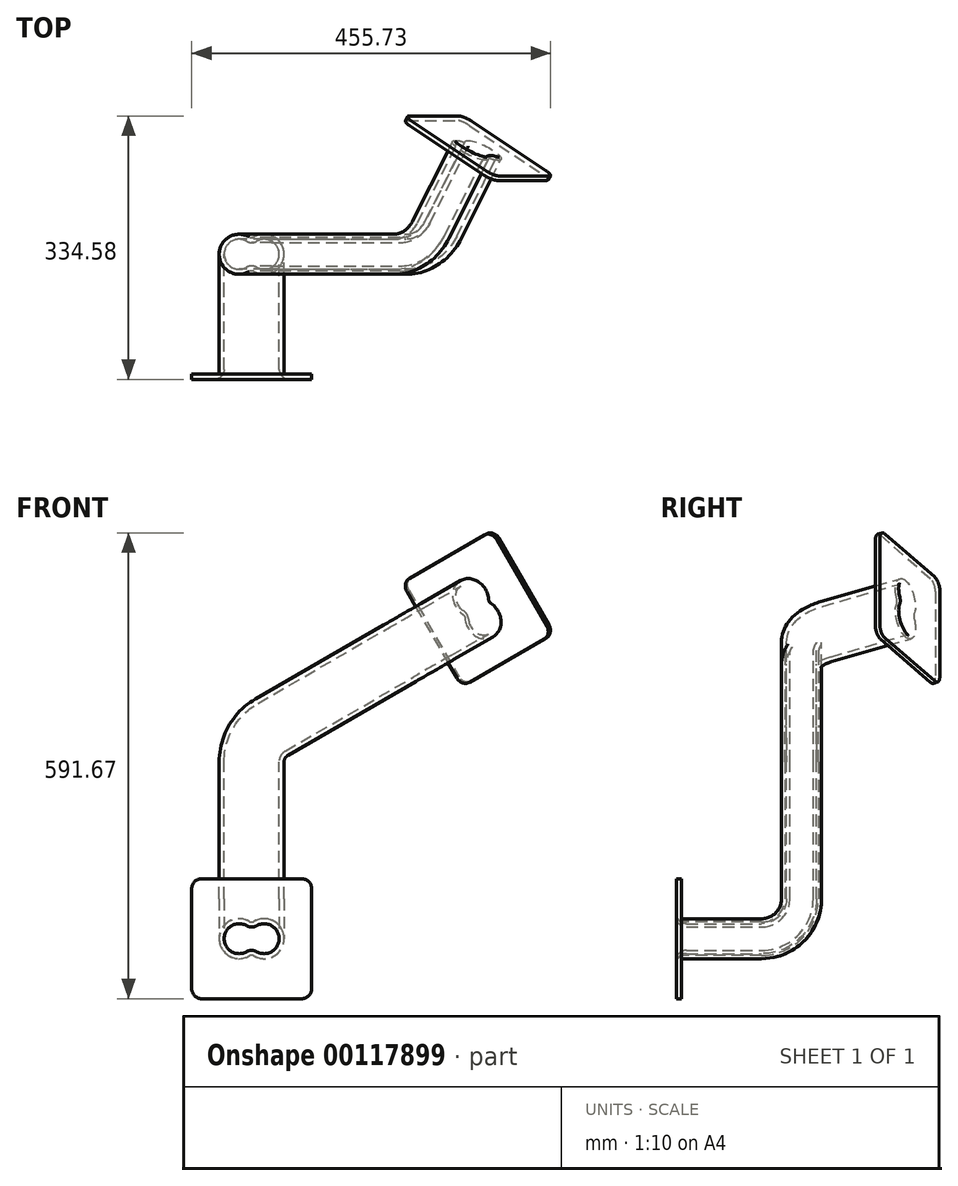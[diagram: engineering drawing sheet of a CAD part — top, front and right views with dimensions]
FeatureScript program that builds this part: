
annotation { "Feature Type Name" : "Feature", "Feature Type Description" : "" }
export const myFeature = defineFeature(function(context is Context, id is Id, definition is map)
    precondition{}
    {
        {
            var Q0;
            Q0=qCreatedBy(makeId("Right.planeOp"),FACE);
            var sketch = newSketch(context, id + "F0", { "sketchPlane" : qUnion([Q0])});
            skLineSegment(sketch, "E0", {"start": v(0, 0) * mm, "end": v(101.6, 0) * mm});
            skLineSegment(sketch, "E1", {"start": v(152.4, 50.8) * mm, "end": v(152.4, 177.8) * mm});
            skPoint(sketch, "E2.visualSharp", {"position": v(152.4, 0) * mm});
            skArc(sketch, "E2.filletArc", {"start": v(101.6, 0) * mm, "mid": v(137.52, 14.88) * mm, "end": v(152.4, 50.8) * mm});
            skSolve(sketch);
        }
        {
            var Q0;
            Q0=qCreatedBy(makeId("Front.planeOp"),FACE);
            var Q1;
            Q1=sQuery(id+"F0.wireOp",VERTEX,"E1.end");
            cPlane(context, id + "F1", {"entities" : qUnion([Q0, Q1]), "cplaneType" : CPlaneType.PLANE_POINT, "offset" : 25.4 * mm, "width" : 152.4 * mm, "height" : 152.4 * mm});
        }
        {
            var Q0;
            Q0=qCreatedBy(id+"F1.planeOp",FACE);
            var sketch = newSketch(context, id + "F2", { "sketchPlane" : qUnion([Q0])});
            skLineSegment(sketch, "E3", {"start": v(0, 177.8) * mm, "end": v(0, 224.67) * mm});
            skLineSegment(sketch, "E4", {"start": v(25.4, 268.66) * mm, "end": v(153.98, 342.9) * mm});
            skPoint(sketch, "E5.visualSharp", {"position": v(0, 254) * mm});
            skArc(sketch, "E5.filletArc", {"start": v(25.4, 268.66) * mm, "mid": v(6.8, 250.07) * mm, "end": v(0, 224.67) * mm});
            skSolve(sketch);
        }
        {
            var Q0;
            Q0=sQuery(id+"F2.wireOp",EDGE,"E4");
            cPlane(context, id + "F3", {"entities" : qUnion([Q0]), "cplaneType" : CPlaneType.LINE_ANGLE, "offset" : 25.4 * mm, "angle" : 90 * degree, "width" : 152.4 * mm, "height" : 152.4 * mm});
        }
        {
            var Q0;
            Q0=qCreatedBy(id+"F3.planeOp",FACE);
            var sketch = newSketch(context, id + "F4", { "sketchPlane" : qUnion([Q0])});
            skLineSegment(sketch, "E6", {"start": v(304.8, 152.4) * mm, "end": v(344.34, 152.4) * mm});
            skLineSegment(sketch, "E7", {"start": v(399.33, 184.15) * mm, "end": v(457.2, 284.38) * mm});
            skPoint(sketch, "E8.visualSharp", {"position": v(381, 152.4) * mm});
            skArc(sketch, "E8.filletArc", {"start": v(344.34, 152.4) * mm, "mid": v(376.09, 160.9) * mm, "end": v(399.33, 184.15) * mm});
            skSolve(sketch);
        }
        {
            var Q0;
            Q0=sQuery(id+"F4.wireOp",EDGE,"E7");
            var Q1;
            Q1=qCreatedBy(id+"F3.planeOp",FACE);
            cPlane(context, id + "F5", {"entities" : qUnion([Q0, Q1]), "cplaneType" : CPlaneType.LINE_ANGLE, "offset" : 25.4 * mm, "angle" : 0 * degree, "width" : 152.4 * mm, "height" : 152.4 * mm});
        }
        {
            var Q0;
            Q0=sQuery(id+"F4.wireOp",VERTEX,"E7.end");
            var Q1;
            Q1=sQuery(id+"F4.wireOp",EDGE,"E7");
            cPlane(context, id + "F6", {"entities" : qUnion([Q0, Q1]), "cplaneType" : CPlaneType.LINE_POINT, "offset" : 25.4 * mm, "width" : 152.4 * mm, "height" : 152.4 * mm});
        }
        {
            var Q0;
            Q0=qCreatedBy(makeId("Front.planeOp"),FACE);
            var sketch = newSketch(context, id + "F7", { "sketchPlane" : qUnion([Q0])});
            skLineSegment(sketch, "E9.bottom", {"start": v(-76.2, 76.2) * mm, "end": v(76.2, 76.2) * mm});
            skLineSegment(sketch, "E9.top", {"start": v(-76.2, -76.2) * mm, "end": v(76.2, -76.2) * mm});
            skLineSegment(sketch, "E9.left", {"start": v(-76.2, 76.2) * mm, "end": v(-76.2, -76.2) * mm});
            skLineSegment(sketch, "E9.right", {"start": v(76.2, 76.2) * mm, "end": v(76.2, -76.2) * mm});
            skSolve(sketch);
        }
        {
            var Q0;
            Q0=qCreatedBy(id+"F6.planeOp",FACE);
            var sketch = newSketch(context, id + "F8", { "sketchPlane" : qUnion([Q0])});
            skLineSegment(sketch, "E10", {"start": v(-110.25, 429.46) * mm, "end": v(16.55, 344.92) * mm});
            skLineSegment(sketch, "E11", {"start": v(16.55, 344.92) * mm, "end": v(-67.99, 218.11) * mm});
            skLineSegment(sketch, "E12", {"start": v(-67.99, 218.11) * mm, "end": v(-194.8, 302.65) * mm});
            skLineSegment(sketch, "E13", {"start": v(-194.8, 302.65) * mm, "end": v(-110.25, 429.46) * mm});
            skSolve(sketch);
        }
        {
            var Q0;
            Q0=qCreatedBy(makeId("Front.planeOp"),FACE);
            var sketch = newSketch(context, id + "F9", { "sketchPlane" : qUnion([Q0])});
            skArc(sketch, "E14", {"start": v(0, 19.83) * mm, "mid": v(-41.27, 0) * mm, "end": v(0, -19.83) * mm});
            skArc(sketch, "E15", {"start": v(0, -19.83) * mm, "mid": v(41.27, 0) * mm, "end": v(0, 19.83) * mm});
            skArc(sketch, "E16", {"start": v(0, 10.53) * mm, "mid": v(-34.92, 0) * mm, "end": v(0, -10.53) * mm});
            skArc(sketch, "E17", {"start": v(0, -10.53) * mm, "mid": v(34.92, 0) * mm, "end": v(0, 10.53) * mm});
            skSolve(sketch);
        }
        {
            var Q0;
            Q0 = qSketchRegion(id + "F9", true);
            var Q1;
            Q1=sQuery(id+"F0.wireOp",EDGE,"E0");
            var Q2;
            Q2=sQuery(id+"F0.wireOp",EDGE,"E2.filletArc");
            var Q3;
            Q3=sQuery(id+"F0.wireOp",EDGE,"E1");
            var Q4;
            Q4=sQuery(id+"F2.wireOp",EDGE,"E5.filletArc");
            var Q5;
            Q5=sQuery(id+"F2.wireOp",EDGE,"E3");
            var Q6;
            Q6=sQuery(id+"F2.wireOp",EDGE,"E4");
            var Q7;
            Q7=sQuery(id+"F4.wireOp",EDGE,"E6");
            var Q8;
            Q8=sQuery(id+"F4.wireOp",EDGE,"E8.filletArc");
            var Q9;
            Q9=sQuery(id+"F4.wireOp",EDGE,"E7");
            sweep(context, id + "F10", {"profiles" : qUnion([Q0]), "path" : qUnion([Q1, Q2, Q3, Q4, Q5, Q6, Q7, Q8, Q9])});
        }
        {
            var Q0;
            Q0=qCreatedBy(makeId("Front.planeOp"),FACE);
            var sketch = newSketch(context, id + "F11", { "sketchPlane" : qUnion([Q0])});
            skArc(sketch, "E18", {"start": v(0, 10.53) * mm, "mid": v(-34.92, 0) * mm, "end": v(0, -10.53) * mm});
            skArc(sketch, "E19", {"start": v(0, -10.53) * mm, "mid": v(34.92, 0) * mm, "end": v(0, 10.53) * mm});
            skSolve(sketch);
        }
        {
            var Q0;
            Q0=qCreatedBy(id+"F6.planeOp",FACE);
            var sketch = newSketch(context, id + "F12", { "sketchPlane" : qUnion([Q0])});
            skArc(sketch, "E20", {"start": v(-97.88, 329.63) * mm, "mid": v(-108.5, 294.73) * mm, "end": v(-80.36, 317.94) * mm});
            skArc(sketch, "E21", {"start": v(-80.36, 317.94) * mm, "mid": v(-69.75, 352.84) * mm, "end": v(-97.88, 329.63) * mm});
            skSolve(sketch);
        }
        {
            var Q0;
            Q0=makeQuery(id+"F7.imprint","IMPRINT",FACE,{"disambiguationData":[TD([[makeQuery(id+"F7.imprint","IMPRINT",EDGE,{"derivedFrom":sQuery(id+"F7.wireOp",EDGE,"E9.bottom")}),-1.0]])]});
            extrude(context, id + "F13", {"entities" : qUnion([Q0]), "depth" : 6.6 * mm, "offsetDistance" : 25.4 * mm});
        }
        {
            var Q0;
            Q0=makeQuery(id+"F8.imprint","IMPRINT",FACE,{"disambiguationData":[TD([[makeQuery(id+"F8.imprint","IMPRINT",EDGE,{"derivedFrom":sQuery(id+"F8.wireOp",EDGE,"E10")}),-1.0]])]});
            extrude(context, id + "F14", {"entities" : qUnion([Q0]), "depth" : 6.35 * mm, "offsetDistance" : 25.4 * mm});
        }
        {
            var Q0;
            Q0 = qSketchRegion(id + "F11", true);
            extrude(context, id + "F15", {"entities" : qUnion([Q0]), "operationType" : NewBodyOperationType.REMOVE, "depth" : 25.4 * mm, "offsetDistance" : 25.4 * mm});
        }
        {
            var Q0;
            Q0 = qSketchRegion(id + "F12", true);
            var Q1;
            Q1=makeQuery(id+"F14.opExtrude","CAP_FACE",FACE,{"disambiguationData":[OSD([sQuery(id+"F8.wireOp",EDGE,"E10"),sQuery(id+"F8.wireOp",EDGE,"E11"),sQuery(id+"F8.wireOp",EDGE,"E12"),sQuery(id+"F8.wireOp",EDGE,"E13")])],"isStart":false});
            extrude(context, id + "F16", {"entities" : qUnion([Q0, Q1]), "operationType" : NewBodyOperationType.REMOVE, "depth" : 25.4 * mm, "offsetDistance" : 25.4 * mm});
        }
        {
            var Q0;
            Q0=makeQuery(id+"F10.opSweep","SWEPT_BODY",BODY,{"disambiguationData":[OSD([sQuery(id+"F4.wireOp",EDGE,"E7"),sQuery(id+"F9.wireOp",EDGE,"E14"),sQuery(id+"F9.wireOp",EDGE,"E15"),sQuery(id+"F9.wireOp",EDGE,"E16"),sQuery(id+"F9.wireOp",EDGE,"E17")])]});
            var Q1;
            Q1=makeQuery(id+"F13.opExtrude","SWEPT_BODY",BODY,{"disambiguationData":[OSD([sQuery(id+"F7.wireOp",EDGE,"E9.bottom"),sQuery(id+"F7.wireOp",EDGE,"E9.top"),sQuery(id+"F7.wireOp",EDGE,"E9.left"),sQuery(id+"F7.wireOp",EDGE,"E9.right")])]});
            var Q2;
            Q2=makeQuery(id+"F14.opExtrude","SWEPT_BODY",BODY,{"disambiguationData":[OSD([sQuery(id+"F8.wireOp",EDGE,"E10"),sQuery(id+"F8.wireOp",EDGE,"E11"),sQuery(id+"F8.wireOp",EDGE,"E12"),sQuery(id+"F8.wireOp",EDGE,"E13")])]});
            booleanBodies(context, id + "F17", {"operationType" : BooleanOperationType.UNION, "tools" : qUnion([Q0, Q1, Q2])});
        }
        {
            var Q0;
            {var subQ0=sQuery(id+"F9.wireOp",EDGE,"E15");var subQ1=sQuery(id+"F9.wireOp",EDGE,"E14");var subQ2=sQuery(id+"F0.wireOp",EDGE,"E1");Q0=makeQuery(id+"F10.opSweep","SWEPT_EDGE",EDGE,{"disambiguationData":[OSD([subQ2,subQ1,subQ0]),TDD([subQ2,makeQuery(id+"F9.imprint","INTERSECT",VERTEX,{"disambiguationData":[OD(0.0)],"derivedFrom":[subQ1,subQ0]})])]});}
            var Q1;
            {var subQ0=sQuery(id+"F9.wireOp",EDGE,"E15");var subQ1=sQuery(id+"F9.wireOp",EDGE,"E14");var subQ2=sQuery(id+"F0.wireOp",EDGE,"E2.filletArc");Q1=makeQuery(id+"F10.opSweep","SWEPT_EDGE",EDGE,{"disambiguationData":[OSD([subQ2,subQ1,subQ0]),TDD([subQ2,makeQuery(id+"F9.imprint","INTERSECT",VERTEX,{"disambiguationData":[OD(1.0)],"derivedFrom":[subQ1,subQ0]})])]});}
            var Q2;
            Q2=makeQuery(id+"F10.opSweep","CAP_EDGE",EDGE,{"disambiguationData":[OSD([sQuery(id+"F4.wireOp",VERTEX,"E7.end"),sQuery(id+"F9.wireOp",EDGE,"E14")])],"isStart":false});
            var Q3;
            Q3=makeQuery(id+"F10.opSweep","CAP_EDGE",EDGE,{"disambiguationData":[OSD([sQuery(id+"F4.wireOp",VERTEX,"E7.end"),sQuery(id+"F9.wireOp",EDGE,"E15")])],"isStart":false});
            var Q4;
            Q4=makeQuery(id+"F10.opSweep","CAP_EDGE",EDGE,{"disambiguationData":[OSD([sQuery(id+"F0.wireOp",VERTEX,"E0.start"),sQuery(id+"F9.wireOp",EDGE,"E14")])],"isStart":true});
            var Q5;
            Q5=makeQuery(id+"F10.opSweep","CAP_EDGE",EDGE,{"disambiguationData":[OSD([sQuery(id+"F0.wireOp",VERTEX,"E0.start"),sQuery(id+"F9.wireOp",EDGE,"E15")])],"isStart":true});
            fillet(context, id + "F18", {"entities" : qUnion([Q0, Q1, Q2, Q3, Q4, Q5]), "tangentPropagation" : true, "radius" : 6.35 * mm, "defaultsChanged" : false, "vertexSettings" : [], "allowEdgeOverflow" : false});
        }
        {
            var Q0;
            {var subQ0=sQuery(id+"F11.wireOp",EDGE,"E19");var subQ1=sQuery(id+"F11.wireOp",EDGE,"E18");var subQ2=sQuery(id+"F9.wireOp",EDGE,"E17");var subQ3=sQuery(id+"F9.wireOp",EDGE,"E16");var subQ4=sQuery(id+"F0.wireOp",EDGE,"E0");Q0=makeQuery(id+"F17.opBoolean","MERGE",EDGE,{"derivedFrom":[makeQuery(id+"F10.opSweep","SWEPT_EDGE",EDGE,{"disambiguationData":[OSD([subQ4,subQ3,subQ2]),TDD([subQ4,makeQuery(id+"F9.imprint","INTERSECT",VERTEX,{"disambiguationData":[OD(1.0)],"derivedFrom":[subQ3,subQ2]})])]}),makeQuery(id+"F15.boolean.opBoolean","COPY",EDGE,{"derivedFrom":makeQuery(id+"F15.opExtrude","SWEPT_EDGE",EDGE,{"disambiguationData":[OSD([subQ1,subQ0]),TDD([makeQuery(id+"F11.imprint","INTERSECT",VERTEX,{"disambiguationData":[OD(1.0)],"derivedFrom":[subQ1,subQ0]})])]})})]});}
            var Q1;
            {var subQ0=sQuery(id+"F11.wireOp",EDGE,"E19");var subQ1=sQuery(id+"F11.wireOp",EDGE,"E18");var subQ2=sQuery(id+"F9.wireOp",EDGE,"E17");var subQ3=sQuery(id+"F9.wireOp",EDGE,"E16");var subQ4=sQuery(id+"F0.wireOp",EDGE,"E0");Q1=makeQuery(id+"F17.opBoolean","MERGE",EDGE,{"derivedFrom":[makeQuery(id+"F10.opSweep","SWEPT_EDGE",EDGE,{"disambiguationData":[OSD([subQ4,subQ3,subQ2]),TDD([subQ4,makeQuery(id+"F9.imprint","INTERSECT",VERTEX,{"disambiguationData":[OD(0.0)],"derivedFrom":[subQ3,subQ2]})])]}),makeQuery(id+"F15.boolean.opBoolean","COPY",EDGE,{"derivedFrom":makeQuery(id+"F15.opExtrude","SWEPT_EDGE",EDGE,{"disambiguationData":[OSD([subQ1,subQ0]),TDD([makeQuery(id+"F11.imprint","INTERSECT",VERTEX,{"disambiguationData":[OD(0.0)],"derivedFrom":[subQ1,subQ0]})])]})})]});}
            var Q2;
            Q2=makeQuery(id+"F15.boolean.opBoolean","INTERSECT",EDGE,{"derivedFrom":[makeQuery(id+"F13.opExtrude","CAP_FACE",FACE,{"disambiguationData":[OSD([sQuery(id+"F7.wireOp",EDGE,"E9.bottom"),sQuery(id+"F7.wireOp",EDGE,"E9.top"),sQuery(id+"F7.wireOp",EDGE,"E9.left"),sQuery(id+"F7.wireOp",EDGE,"E9.right")])],"isStart":false}),makeQuery(id+"F15.opExtrude","SWEPT_FACE",FACE,{"disambiguationData":[OSD([sQuery(id+"F11.wireOp",EDGE,"E19")])]})]});
            var Q3;
            Q3=makeQuery(id+"F15.boolean.opBoolean","INTERSECT",EDGE,{"derivedFrom":[makeQuery(id+"F13.opExtrude","CAP_FACE",FACE,{"disambiguationData":[OSD([sQuery(id+"F7.wireOp",EDGE,"E9.bottom"),sQuery(id+"F7.wireOp",EDGE,"E9.top"),sQuery(id+"F7.wireOp",EDGE,"E9.left"),sQuery(id+"F7.wireOp",EDGE,"E9.right")])],"isStart":false}),makeQuery(id+"F15.opExtrude","SWEPT_FACE",FACE,{"disambiguationData":[OSD([sQuery(id+"F11.wireOp",EDGE,"E18")])]})]});
            var Q4;
            {var subQ0=sQuery(id+"F8.wireOp",EDGE,"E13");var subQ1=sQuery(id+"F8.wireOp",EDGE,"E12");var subQ2=sQuery(id+"F8.wireOp",EDGE,"E11");var subQ3=sQuery(id+"F8.wireOp",EDGE,"E10");Q4=makeQuery(id+"F16.boolean.opBoolean","INTERSECT",EDGE,{"derivedFrom":[makeQuery(id+"F14.opExtrude","CAP_FACE",FACE,{"disambiguationData":[OSD([subQ3,subQ2,subQ1,subQ0])],"isStart":false}),makeQuery(id+"F16.opExtrude","SWEPT_FACE",FACE,{"disambiguationData":[OSD([sQuery(id+"F12.wireOp",EDGE,"E20")])]}),makeQuery(id+"F16.opExtrude","CAP_FACE",FACE,{"disambiguationData":[OSD([subQ3,subQ2,subQ1,subQ0])],"isStart":true})]});}
            var Q5;
            {var subQ0=sQuery(id+"F8.wireOp",EDGE,"E13");var subQ1=sQuery(id+"F8.wireOp",EDGE,"E12");var subQ2=sQuery(id+"F8.wireOp",EDGE,"E11");var subQ3=sQuery(id+"F8.wireOp",EDGE,"E10");Q5=makeQuery(id+"F16.boolean.opBoolean","INTERSECT",EDGE,{"derivedFrom":[makeQuery(id+"F14.opExtrude","CAP_FACE",FACE,{"disambiguationData":[OSD([subQ3,subQ2,subQ1,subQ0])],"isStart":false}),makeQuery(id+"F16.opExtrude","SWEPT_FACE",FACE,{"disambiguationData":[OSD([sQuery(id+"F12.wireOp",EDGE,"E21")])]}),makeQuery(id+"F16.opExtrude","CAP_FACE",FACE,{"disambiguationData":[OSD([subQ3,subQ2,subQ1,subQ0])],"isStart":true})]});}
            fillet(context, id + "F19", {"entities" : qUnion([Q0, Q1, Q2, Q3, Q4, Q5]), "tangentPropagation" : true, "radius" : 12.7 * mm, "defaultsChanged" : false, "vertexSettings" : [], "allowEdgeOverflow" : false});
        }
        {
            var Q0;
            Q0=makeQuery(id+"F13.opExtrude","SWEPT_EDGE",EDGE,{"disambiguationData":[OSD([sQuery(id+"F7.wireOp",EDGE,"E9.bottom"),sQuery(id+"F7.wireOp",EDGE,"E9.left")])]});
            var Q1;
            Q1=makeQuery(id+"F13.opExtrude","SWEPT_EDGE",EDGE,{"disambiguationData":[OSD([sQuery(id+"F7.wireOp",EDGE,"E9.top"),sQuery(id+"F7.wireOp",EDGE,"E9.left")])]});
            var Q2;
            Q2=makeQuery(id+"F13.opExtrude","SWEPT_EDGE",EDGE,{"disambiguationData":[OSD([sQuery(id+"F7.wireOp",EDGE,"E9.top"),sQuery(id+"F7.wireOp",EDGE,"E9.right")])]});
            var Q3;
            Q3=makeQuery(id+"F13.opExtrude","SWEPT_EDGE",EDGE,{"disambiguationData":[OSD([sQuery(id+"F7.wireOp",EDGE,"E9.bottom"),sQuery(id+"F7.wireOp",EDGE,"E9.right")])]});
            var Q4;
            Q4=makeQuery(id+"F14.opExtrude","SWEPT_EDGE",EDGE,{"disambiguationData":[OSD([sQuery(id+"F8.wireOp",EDGE,"E11"),sQuery(id+"F8.wireOp",EDGE,"E12")])]});
            var Q5;
            Q5=makeQuery(id+"F14.opExtrude","SWEPT_EDGE",EDGE,{"disambiguationData":[OSD([sQuery(id+"F8.wireOp",EDGE,"E12"),sQuery(id+"F8.wireOp",EDGE,"E13")])]});
            var Q6;
            Q6=makeQuery(id+"F14.opExtrude","SWEPT_EDGE",EDGE,{"disambiguationData":[OSD([sQuery(id+"F8.wireOp",EDGE,"E10"),sQuery(id+"F8.wireOp",EDGE,"E13")])]});
            var Q7;
            Q7=makeQuery(id+"F14.opExtrude","SWEPT_EDGE",EDGE,{"disambiguationData":[OSD([sQuery(id+"F8.wireOp",EDGE,"E10"),sQuery(id+"F8.wireOp",EDGE,"E11")])]});
            fillet(context, id + "F20", {"entities" : qUnion([Q0, Q1, Q2, Q3, Q4, Q5, Q6, Q7]), "tangentPropagation" : true, "radius" : 12.7 * mm, "defaultsChanged" : false, "vertexSettings" : [], "allowEdgeOverflow" : false});
        }
    });
